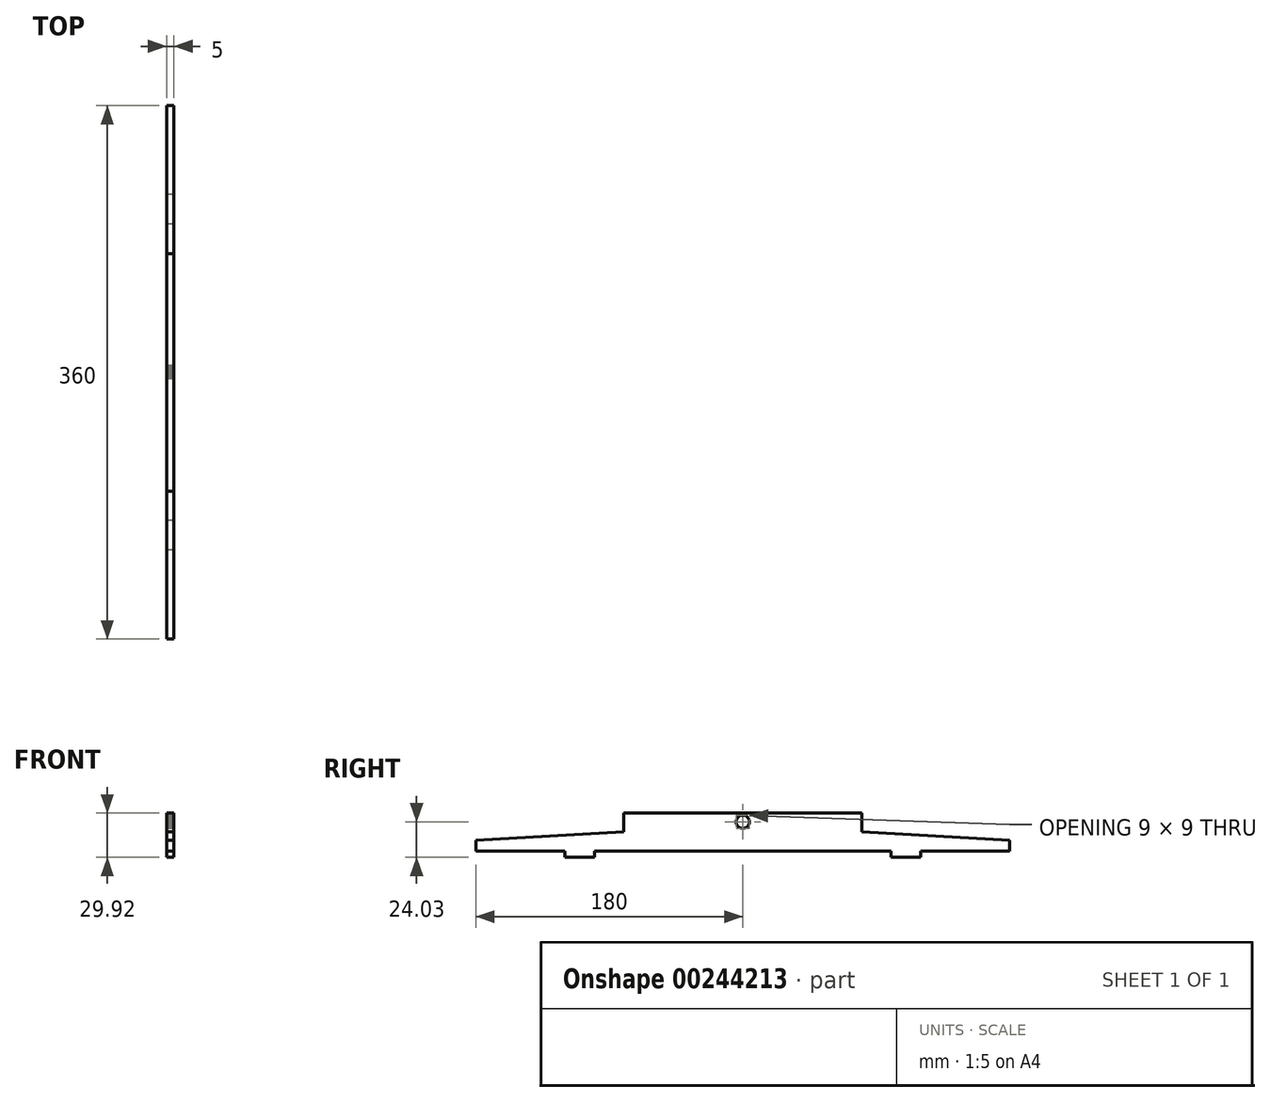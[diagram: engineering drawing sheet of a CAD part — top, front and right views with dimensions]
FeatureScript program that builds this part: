
annotation { "Feature Type Name" : "Feature", "Feature Type Description" : "" }
export const myFeature = defineFeature(function(context is Context, id is Id, definition is map)
    precondition{}
    {
        {
            var Q0;
            Q0=qCreatedBy(makeId("Right.planeOp"),FACE);
            var sketch = newSketch(context, id + "F0", { "sketchPlane" : qUnion([Q0])});
            skLineSegment(sketch, "E0", {"start": v(-80.2, 14.96) * mm, "end": v(80.2, 14.96) * mm});
            skLineSegment(sketch, "E1", {"start": v(80.2, 14.96) * mm, "end": v(80.2, 2.18) * mm});
            skLineSegment(sketch, "E2", {"start": v(80.2, 2.18) * mm, "end": v(180, -3.26) * mm});
            skLineSegment(sketch, "E3", {"start": v(180, -3.26) * mm, "end": v(180, -10.76) * mm});
            skLineSegment(sketch, "E4", {"start": v(180, -10.76) * mm, "end": v(120, -10.76) * mm});
            skLineSegment(sketch, "E5", {"start": v(120, -10.76) * mm, "end": v(120, -14.96) * mm});
            skLineSegment(sketch, "E6", {"start": v(120, -14.96) * mm, "end": v(100, -14.96) * mm});
            skLineSegment(sketch, "E7", {"start": v(100, -14.96) * mm, "end": v(100, -10.76) * mm});
            skLineSegment(sketch, "E8", {"start": v(100, -10.76) * mm, "end": v(-100, -10.76) * mm});
            skLineSegment(sketch, "E9", {"start": v(-100, -10.76) * mm, "end": v(-100, -14.96) * mm});
            skLineSegment(sketch, "E10", {"start": v(-100, -14.96) * mm, "end": v(-120, -14.96) * mm});
            skLineSegment(sketch, "E11", {"start": v(-120, -14.96) * mm, "end": v(-120, -10.76) * mm});
            skLineSegment(sketch, "E12", {"start": v(-120, -10.76) * mm, "end": v(-180, -10.76) * mm});
            skLineSegment(sketch, "E13", {"start": v(-180, -10.76) * mm, "end": v(-180, -3.26) * mm});
            skLineSegment(sketch, "E14", {"start": v(-180, -3.26) * mm, "end": v(-80.2, 2.18) * mm});
            skLineSegment(sketch, "E15", {"start": v(-80.2, 2.18) * mm, "end": v(-80.2, 14.96) * mm});
            skLineSegment(sketch, "E16", {"start": v(0, 4.57) * mm, "end": v(1.16, 4.72) * mm});
            skLineSegment(sketch, "E17", {"start": v(1.16, 4.72) * mm, "end": v(2.25, 5.17) * mm});
            skLineSegment(sketch, "E18", {"start": v(2.25, 5.17) * mm, "end": v(3.18, 5.89) * mm});
            skLineSegment(sketch, "E19", {"start": v(3.18, 5.89) * mm, "end": v(3.9, 6.82) * mm});
            skLineSegment(sketch, "E20", {"start": v(3.9, 6.82) * mm, "end": v(4.35, 7.9) * mm});
            skLineSegment(sketch, "E21", {"start": v(4.35, 7.9) * mm, "end": v(4.5, 9.07) * mm});
            skLineSegment(sketch, "E22", {"start": v(4.5, 9.07) * mm, "end": v(4.35, 10.23) * mm});
            skLineSegment(sketch, "E23", {"start": v(4.35, 10.23) * mm, "end": v(3.9, 11.32) * mm});
            skLineSegment(sketch, "E24", {"start": v(3.9, 11.32) * mm, "end": v(3.18, 12.25) * mm});
            skLineSegment(sketch, "E25", {"start": v(3.18, 12.25) * mm, "end": v(2.25, 12.97) * mm});
            skLineSegment(sketch, "E26", {"start": v(2.25, 12.97) * mm, "end": v(1.16, 13.42) * mm});
            skLineSegment(sketch, "E27", {"start": v(1.16, 13.42) * mm, "end": v(0, 13.57) * mm});
            skLineSegment(sketch, "E28", {"start": v(0, 13.57) * mm, "end": v(-1.16, 13.42) * mm});
            skLineSegment(sketch, "E29", {"start": v(-1.16, 13.42) * mm, "end": v(-2.25, 12.97) * mm});
            skLineSegment(sketch, "E30", {"start": v(-2.25, 12.97) * mm, "end": v(-3.18, 12.25) * mm});
            skLineSegment(sketch, "E31", {"start": v(-3.18, 12.25) * mm, "end": v(-3.9, 11.32) * mm});
            skLineSegment(sketch, "E32", {"start": v(-3.9, 11.32) * mm, "end": v(-4.35, 10.23) * mm});
            skLineSegment(sketch, "E33", {"start": v(-4.35, 10.23) * mm, "end": v(-4.5, 9.07) * mm});
            skLineSegment(sketch, "E34", {"start": v(-4.5, 9.07) * mm, "end": v(-4.35, 7.9) * mm});
            skLineSegment(sketch, "E35", {"start": v(-4.35, 7.9) * mm, "end": v(-3.9, 6.82) * mm});
            skLineSegment(sketch, "E36", {"start": v(-3.9, 6.82) * mm, "end": v(-3.18, 5.89) * mm});
            skLineSegment(sketch, "E37", {"start": v(-3.18, 5.89) * mm, "end": v(-2.25, 5.17) * mm});
            skLineSegment(sketch, "E38", {"start": v(-2.25, 5.17) * mm, "end": v(-1.16, 4.72) * mm});
            skLineSegment(sketch, "E39", {"start": v(-1.16, 4.72) * mm, "end": v(0, 4.57) * mm});
            skSolve(sketch);
        }
        {
            var Q0;
            Q0 = qSketchRegion(id + "F0", true);
            extrude(context, id + "F1", {"entities" : qUnion([Q0]), "depth" : 5 * mm});
        }
    });
